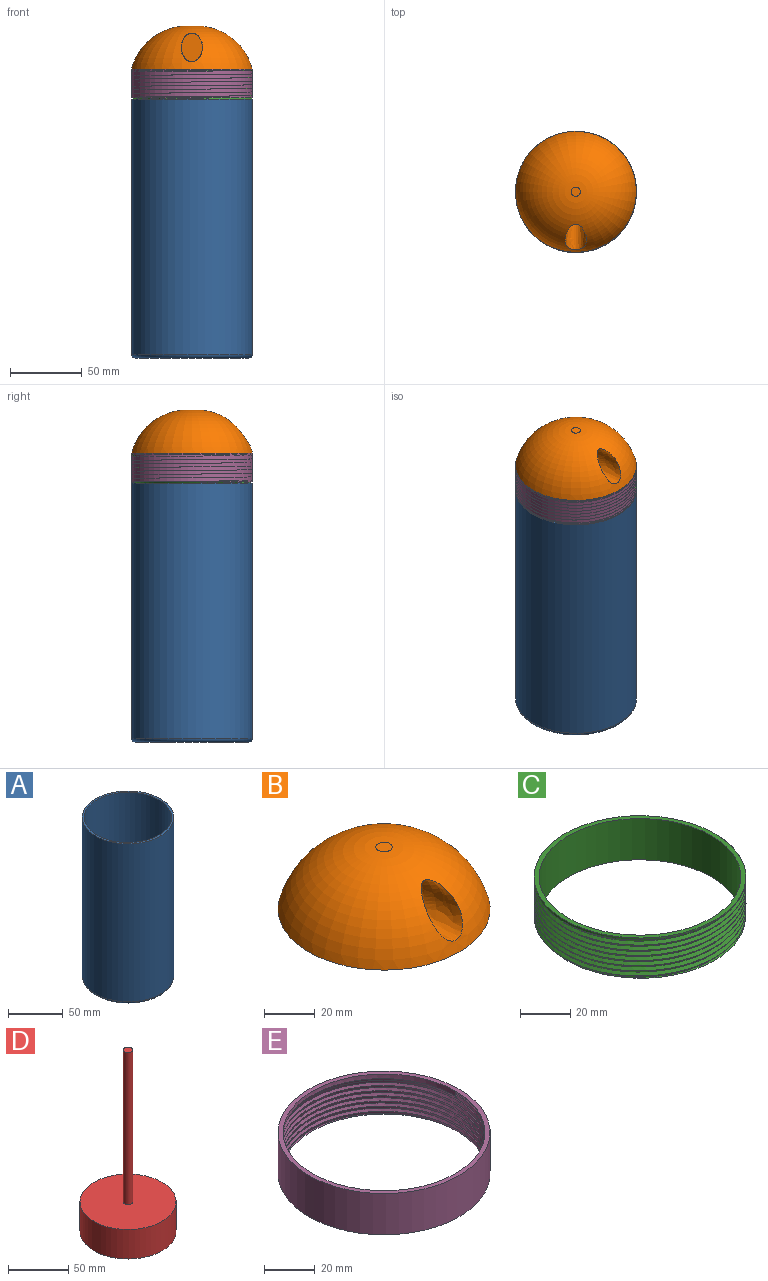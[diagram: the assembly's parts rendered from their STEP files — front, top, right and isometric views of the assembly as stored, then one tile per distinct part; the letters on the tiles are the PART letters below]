
ASSEMBLY  parts=5 mates=3
PART A: 6 faces, bbox 90.9x90.9x180 mm
  f0: cylinder r=42mm len=177.5mm, axis (0,0,1), area 46841.1mm2, adj f2,f5
  f1: plane 79x79mm, normal (0,0,-1), area 4901.7mm2, adj f5
  f2: plane 84x84mm, normal (0,0,1), area 515.2mm2, adj f0,f3
  f3: cylinder r=40mm len=176mm, axis (0,0,1), area 44233.6mm2, adj f2,f4
  f4: plane 80x80mm, normal (0,0,1), area 5026.5mm2, adj f3
  f5: torus R=39.5mm, axis (0,0,1), area 1013.9mm2, adj f0,f1
PART B: 5 faces, bbox 84x84x30 mm
  f0: torus R=3.27mm, axis (0,0,-1), area 8304.5mm2, adj f1,f2,f3
  f1: plane 6.54x6.54mm, normal (0,0,1), area 33.6mm2, adj f0
  f2: plane 84x84mm, normal (0,0,-1), area 5541.8mm2, adj f0
  f3: extruded ~40.32x20mm, area 1802.4mm2, adj f0,f4
  f4: plane 20x15mm, normal (0,-1,0), area 235.6mm2, adj f3
PART C: 7 faces, bbox 84x97x21.7 mm
  f0: cylinder r=42mm len=84mm, axis (0,0,-1), area 90.1mm2, adj f1,f2,f3,f4,f5
  f1: plane 84x84mm, normal (0,0,1), area 515.2mm2, adj f0,f6
  f2: plane 83.05x83.04mm, normal (0,0,-1), area 388.8mm2, adj f0,f3,f4,f6
  f3: bspline ~97x84mm, area 3202.5mm2, adj f0,f2,f4,f5
  f4: bspline ~97x84mm, area 3001.3mm2, adj f0,f2,f3,f5
  f5: plane 2.49x0.97mm, normal (0,-1,0), area 1.2mm2, adj f0,f3,f4
  f6: cylinder r=40mm len=80mm, axis (0,0,-1), area 5026.5mm2, adj f1,f2
PART D: 5 faces, bbox 80x80x185 mm
  f0: cylinder r=40mm len=80mm, axis (0,0,-1), area 7539.8mm2, adj f1,f2
  f1: plane 80x80mm, normal (0,0,1), area 4976.3mm2, adj f0,f3
  f2: plane 80x80mm, normal (0,0,-1), area 5026.5mm2, adj f0
  f3: cylinder r=4mm len=155mm, axis (0,0,-1), area 3895.6mm2, adj f1,f4
  f4: plane 8x8mm, normal (0,0,1), area 50.3mm2, adj f3
PART E: 8 faces, bbox 85x95.7x22.7 mm
  f0: cylinder r=42mm len=84mm, axis (0,0,-1), area 5277.9mm2, adj f1,f2
  f1: plane 84x84mm, normal (0,0,1), area 515.2mm2, adj f0,f3
  f2: plane 85.04x85.04mm, normal (0,0,-1), area 332.7mm2, adj f0,f4,f5
  f3: cylinder r=40mm len=80mm, axis (0,0,-1), area 314.2mm2, adj f1,f6,f7
  f4: bspline ~94.62x81.94mm, area 2561.2mm2, adj f2,f5,f6,f7
  f5: bspline ~94.62x81.94mm, area 2271.2mm2, adj f2,f4,f6
  f6: plane 3.71x0.97mm, normal (0,-1,0), area 1.8mm2, adj f3,f4,f5,f7
  f7: bspline ~93.46x80.94mm, area 328mm2, adj f3,f4,f6
PLACE A t=(6.07,-29.24,-157.87)mm
PLACE B t=(5.95,-29.27,-137.06)mm
PLACE C t=(6.07,-29.24,-157.87)mm
PLACE D t=(5.95,-29.27,-322.06)mm
PLACE E t=(5.95,-29.27,-157.06)mm
MATE fastened A.f0 <-> C.f0  axis (0,0,1) through (6.07,-29.24,-157.87)mm
MATE fastened D.f0 <-> B.f0  axis (0,0,1) through (5.95,-29.27,-137.06)mm
MATE fastened E.f0 <-> B.f0  axis (0,0,-1) through (5.95,-29.27,-137.06)mm
